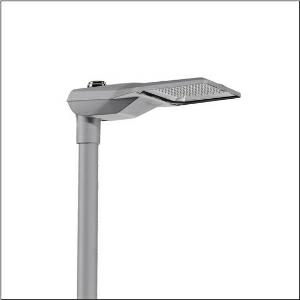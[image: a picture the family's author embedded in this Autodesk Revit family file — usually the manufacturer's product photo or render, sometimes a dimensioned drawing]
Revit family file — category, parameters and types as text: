
# Revit family: streetlight_sl_21_midi___p1_0a_5xe7a47n08lb_4b2d
name_source: partatom
category: Lighting Fixtures
units: mm (PartAtom-declared; Revit-internal decimal feet)

## family parameters
Cut with Voids When Loaded = No
Host = Face
Light Source = No
Part Type = Normal
Room Calculation Point = No
Round Connector Dimension = Use Diameter
Shared = No

## types (1)
- --- (1 x LED, 14950 lm, 98.3 W, 4000K)
    Apparent Load = 98 VA
    CIE Flux Codes = 21 50 90 100 100
    Color Rendering = 70
    Color Temperature = 4000K
    Default Elevation = 1800 mm
    Description = Streetlight SL 21 midi, mast luminaire, primary light control with lens, of PMMA, primary optical cover: cover, of toughened safety glass, transparent, light distribution: P1.0a, light emission: direct distribution, primary light characteristic: asymmetric, installation type: side-entry, LED, 3G 2.5mm², High Power LED, rated luminous flux: 14.950lm, luminous efficacy: 152lm/W, light colour: 740, colour temperature: 4000K, control gear: NEMA (7pin), control: overheat protection, pre-setting: linear dimming characteristic, constant luminous flux control, time-dependent luminous flux control, flexible luminous flux parameterisation, mains connection: 220..240V, AC, 50/60Hz, connection cable pre-assembled, cable length: 10,5m, wiring characteristics: H05VV-F, start of lifetime: 98W, end of service life: 101W, reduction: 45W, luminaire housing, of diecast aluminium (EN AC-44300), powder-coated, Siteco® metallic grey (DB 702S), corrosivity category C5 mid according to DIN EN ISO 12944, multi-level sealing system, sealing non-destructively replaceable, inclination adjustable: 0°, 5°, 10°, 15°, length: 644mm, width: 335mm, height: 110mm, spigot size: 42mm (side-entry), mounting height: 4..8m, protection rating (complete): IP66, insulation class (complete): insulation class I (protective earthing), certification: CE, ENEC, ENEC+, VDE, impact resistance: IK10, permissible operating ambient temperature for outdoor applications: -40..+50°C, standard-compliant lighting for roads and squares, packaging unit: 1 piece

Light Distribution: P1.0a
    Height = 111 mm
    Lamp = 1 x LED
    Lamp Light Flux = 14950 lm
    Lamp Power = 98.3 W
    Lamp count = 1
    Length = 644 mm
    Luminous efficacy = 152 lm/W
    Manufacturer = Siteco
    ModVariant = No
    Model = 5XE7A47N08LB
    Number of Poles = 1
    OnlyDefault = Yes
    Power Factor = 1
    Product Name = Streetlight SL 21 midi | P1.0a
    Product group = mast luminaire | pylon top
    ProductGroupID = 6100
    Protection Class = Protection class I
    Protection Degree = IP 66
    RLX_Detail_Level = 1
    RLX_Emergency_Light_Flux = 0 lm
    RLX_Emergency_Type = 0
    RLX_Emergency_Type_DB = No
    RlxData = <blob elided: 37921 chars, md5=8a665a2e>
    Socket = socket
    Standby Power = 0 W
    System Light Flux = 14950 lm
    System Power = 98 W
    Type Comments = factory setting: luminous flux: 100 % | dim-lin: 254 | 1020 mA
    Type Image = l_1294377.jpg
    URL = http://relux.com
    VarID = @adj_155961
    Voltage = 0 V
    Weight = 0.00 kg
    Width = 336 mm

## geometry (parser evidence)
native form markers: Blend x4, Sweep x12
no freeform markers — native parametric forms only
